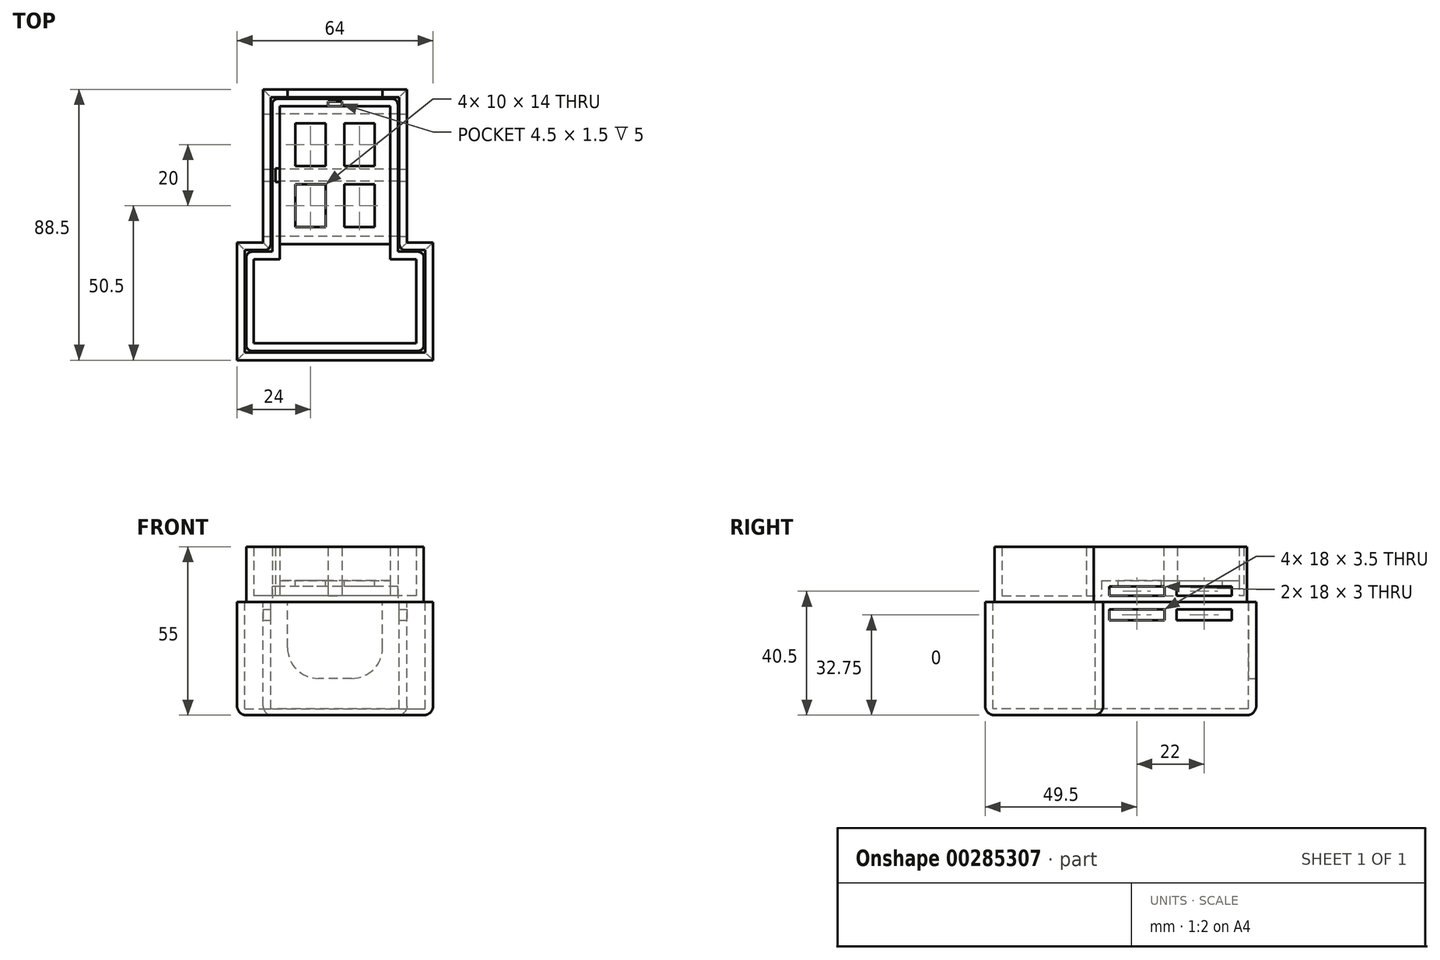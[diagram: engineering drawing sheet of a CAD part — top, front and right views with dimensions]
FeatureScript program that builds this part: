
annotation { "Feature Type Name" : "Feature", "Feature Type Description" : "" }
export const myFeature = defineFeature(function(context is Context, id is Id, definition is map)
    precondition{}
    {
        {
            var Q0;
            Q0=qCreatedBy(makeId("Top.planeOp"),FACE);
            var sketch = newSketch(context, id + "F0", { "sketchPlane" : qUnion([Q0])});
            skLineSegment(sketch, "E0.bottom", {"start": v(20.5, 25) * mm, "end": v(-20.5, 25) * mm});
            skLineSegment(sketch, "E0.left", {"start": v(20.5, 25) * mm, "end": v(20.5, -25) * mm});
            skLineSegment(sketch, "E0.right", {"start": v(-20.5, 25) * mm, "end": v(-20.5, -25) * mm});
            skPoint(sketch, "E0.middle", {"position": v(0, 0) * mm});
            skLineSegment(sketch, "E1.bottom", {"start": v(-29, -25) * mm, "end": v(-20.5, -25) * mm});
            skLineSegment(sketch, "E1.top", {"start": v(-29, -57.5) * mm, "end": v(29, -57.5) * mm});
            skLineSegment(sketch, "E1.left", {"start": v(-29, -25) * mm, "end": v(-29, -57.5) * mm});
            skLineSegment(sketch, "E1.right", {"start": v(29, -25) * mm, "end": v(29, -57.5) * mm});
            skPoint(sketch, "E1.middle", {"position": v(0, -41.25) * mm});
            skLineSegment(sketch, "E2.trimOffspring", {"start": v(20.5, -25) * mm, "end": v(29, -25) * mm});
            skLineSegment(sketch, "E3.0", {"start": v(18, 22.5) * mm, "end": v(2.25, 22.5) * mm});
            skLineSegment(sketch, "E3.1", {"start": v(-18, 22.5) * mm, "end": v(-18, 2.25) * mm});
            skLineSegment(sketch, "E3.2", {"start": v(18, 22.5) * mm, "end": v(18, -27.5) * mm});
            skLineSegment(sketch, "E3.3", {"start": v(-26.5, -27.5) * mm, "end": v(-18, -27.5) * mm});
            skLineSegment(sketch, "E3.4", {"start": v(18, -27.5) * mm, "end": v(26.5, -27.5) * mm});
            skLineSegment(sketch, "E3.5", {"start": v(26.5, -27.5) * mm, "end": v(26.5, -55) * mm});
            skLineSegment(sketch, "E3.6", {"start": v(-26.5, -55) * mm, "end": v(26.5, -55) * mm});
            skLineSegment(sketch, "E3.7", {"start": v(-26.5, -27.5) * mm, "end": v(-26.5, -55) * mm});
            skLineSegment(sketch, "E4.top", {"start": v(-2.25, 24) * mm, "end": v(2.25, 24) * mm});
            skLineSegment(sketch, "E4.left", {"start": v(-2.25, 22.5) * mm, "end": v(-2.25, 24) * mm});
            skLineSegment(sketch, "E4.right", {"start": v(2.25, 22.5) * mm, "end": v(2.25, 24) * mm});
            skLineSegment(sketch, "E5.trimOffspring", {"start": v(-2.25, 22.5) * mm, "end": v(-18, 22.5) * mm});
            skLineSegment(sketch, "E6.bottom", {"start": v(-18, 2.25) * mm, "end": v(-19.5, 2.25) * mm});
            skLineSegment(sketch, "E6.top", {"start": v(-18, -2.25) * mm, "end": v(-19.5, -2.25) * mm});
            skLineSegment(sketch, "E6.right", {"start": v(-19.5, 2.25) * mm, "end": v(-19.5, -2.25) * mm});
            skLineSegment(sketch, "E7.trimOffspring", {"start": v(-18, -2.25) * mm, "end": v(-18, -27.5) * mm});
            skLineSegment(sketch, "E8.0", {"start": v(-29.5, -24.5) * mm, "end": v(-29.5, -58) * mm});
            skLineSegment(sketch, "E8.1", {"start": v(-29.5, -24.5) * mm, "end": v(-23, -24.5) * mm});
            skLineSegment(sketch, "E8.2", {"start": v(-29.5, -58) * mm, "end": v(29.5, -58) * mm});
            skLineSegment(sketch, "E8.3", {"start": v(-21, 25.5) * mm, "end": v(-21, -22.5) * mm});
            skLineSegment(sketch, "E8.4", {"start": v(29.5, -24.5) * mm, "end": v(29.5, -58) * mm});
            skLineSegment(sketch, "E8.5", {"start": v(23, -24.5) * mm, "end": v(29.5, -24.5) * mm});
            skLineSegment(sketch, "E8.6", {"start": v(21, 25.5) * mm, "end": v(21, -22.5) * mm});
            skLineSegment(sketch, "E8.7", {"start": v(21, 25.5) * mm, "end": v(-21, 25.5) * mm});
            skLineSegment(sketch, "E9.0", {"start": v(-32, -22) * mm, "end": v(-32, -60.5) * mm});
            skLineSegment(sketch, "E9.1", {"start": v(-32, -22) * mm, "end": v(-23.5, -22) * mm});
            skLineSegment(sketch, "E9.2", {"start": v(-32, -60.5) * mm, "end": v(32, -60.5) * mm});
            skLineSegment(sketch, "E9.3", {"start": v(-23.5, 28) * mm, "end": v(-23.5, -22) * mm});
            skLineSegment(sketch, "E9.4", {"start": v(32, -22) * mm, "end": v(32, -60.5) * mm});
            skLineSegment(sketch, "E9.5", {"start": v(23.5, -22) * mm, "end": v(32, -22) * mm});
            skLineSegment(sketch, "E9.6", {"start": v(23.5, 28) * mm, "end": v(23.5, -22) * mm});
            skLineSegment(sketch, "E9.7", {"start": v(23.5, 28) * mm, "end": v(-23.5, 28) * mm});
            skPoint(sketch, "E10.visualSharp", {"position": v(-21, -24.5) * mm});
            skArc(sketch, "E10.filletArc", {"start": v(-23, -24.5) * mm, "mid": v(-21.59, -23.91) * mm, "end": v(-21, -22.5) * mm});
            skPoint(sketch, "E11.visualSharp", {"position": v(21, -24.5) * mm});
            skArc(sketch, "E11.filletArc", {"start": v(21, -22.5) * mm, "mid": v(21.59, -23.91) * mm, "end": v(23, -24.5) * mm});
            skSolve(sketch);
        }
        {
            var Q0;
            Q0=makeQuery(id+"F0.imprint","IMPRINT",FACE,{"disambiguationData":[TD([[makeQuery(id+"F0.imprint","IMPRINT",EDGE,{"derivedFrom":sQuery(id+"F0.wireOp",EDGE,"E0.bottom")}),1.0]])]});
            var Q1;
            Q1=makeQuery(id+"F0.imprint","IMPRINT",FACE,{"disambiguationData":[TD([[makeQuery(id+"F0.imprint","IMPRINT",EDGE,{"derivedFrom":sQuery(id+"F0.wireOp",EDGE,"E3.0")}),1.0]])]});
            extrude(context, id + "F1", {"entities" : qUnion([Q0, Q1]), "depth" : 2 * mm});
        }
        {
            var Q0;
            Q0=makeQuery(id+"F0.imprint","IMPRINT",FACE,{"disambiguationData":[TD([[makeQuery(id+"F0.imprint","IMPRINT",EDGE,{"derivedFrom":sQuery(id+"F0.wireOp",EDGE,"E0.bottom")}),1.0]])]});
            extrude(context, id + "F2", {"entities" : qUnion([Q0]), "operationType" : NewBodyOperationType.ADD, "depth" : 18 * mm});
        }
        {
            var Q0;
            Q0=makeQuery(id+"F1.opExtrude","CAP_FACE",FACE,{"disambiguationData":[OSD([sQuery(id+"F0.wireOp",EDGE,"E0.bottom"),sQuery(id+"F0.wireOp",EDGE,"E0.left"),sQuery(id+"F0.wireOp",EDGE,"E0.right"),sQuery(id+"F0.wireOp",EDGE,"E1.bottom"),sQuery(id+"F0.wireOp",EDGE,"E1.top"),sQuery(id+"F0.wireOp",EDGE,"E1.left"),sQuery(id+"F0.wireOp",EDGE,"E1.right"),sQuery(id+"F0.wireOp",EDGE,"E2.trimOffspring")])],"isStart":false});
            var sketch = newSketch(context, id + "F3", { "sketchPlane" : qUnion([Q0])});
            skLineSegment(sketch, "E12.bottom", {"start": v(18, 22.5) * mm, "end": v(-18, 22.5) * mm});
            skLineSegment(sketch, "E12.top", {"start": v(18, -22.5) * mm, "end": v(-18, -22.5) * mm});
            skLineSegment(sketch, "E12.left", {"start": v(18, 22.5) * mm, "end": v(18, -22.5) * mm});
            skLineSegment(sketch, "E12.right", {"start": v(-18, 22.5) * mm, "end": v(-18, -22.5) * mm});
            skPoint(sketch, "E12.middle", {"position": v(0, 0) * mm});
            skSolve(sketch);
        }
        {
            var Q0;
            {var subQ0=sQuery(id+"F3.wireOp",EDGE,"E12.top");Q0=makeQuery(id+"F3.imprint","IMPRINT",FACE,{"disambiguationData":[TD([[makeQuery(id+"F3.imprint","IMPRINT",EDGE,{"derivedFrom":subQ0}),-1.0]])]});}
            extrude(context, id + "F4", {"entities" : qUnion([Q0]), "operationType" : NewBodyOperationType.ADD, "depth" : 5 * mm});
        }
        {
            var Q0;
            {var subQ0=sQuery(id+"F0.wireOp",EDGE,"E0.right");Q0=makeQuery(id+"F2.boolean.opBoolean","MERGE",FACE,{"derivedFrom":[makeQuery(id+"F1.opExtrude","SWEPT_FACE",FACE,{"disambiguationData":[OSD([subQ0])]}),makeQuery(id+"F2.opExtrude","SWEPT_FACE",FACE,{"disambiguationData":[OSD([subQ0])]})]});}
            var sketch = newSketch(context, id + "F5", { "sketchPlane" : qUnion([Q0])});
            skLineSegment(sketch, "E13.bottom", {"start": v(20, 2) * mm, "end": v(2, 2) * mm});
            skLineSegment(sketch, "E13.top", {"start": v(20, 5) * mm, "end": v(2, 5) * mm});
            skLineSegment(sketch, "E13.left", {"start": v(20, 2) * mm, "end": v(20, 5) * mm});
            skLineSegment(sketch, "E13.right", {"start": v(-20, 2) * mm, "end": v(-20, 5) * mm});
            skLineSegment(sketch, "E14", {"start": v(-2, 5) * mm, "end": v(-2, 2) * mm});
            skLineSegment(sketch, "E15", {"start": v(2, 5) * mm, "end": v(2, 2) * mm});
            skLineSegment(sketch, "E16.trimOffspring", {"start": v(-2, 5) * mm, "end": v(-20, 5) * mm});
            skLineSegment(sketch, "E17.trimOffspring", {"start": v(-2, 2) * mm, "end": v(-20, 2) * mm});
            skSolve(sketch);
        }
        {
            var Q0;
            Q0 = qSketchRegion(id + "F5", true);
            var Q1;
            {var subQ0=sQuery(id+"F0.wireOp",EDGE,"E0.left");Q1=makeQuery(id+"F2.boolean.opBoolean","MERGE",FACE,{"derivedFrom":[makeQuery(id+"F1.opExtrude","SWEPT_FACE",FACE,{"disambiguationData":[OSD([subQ0])]}),makeQuery(id+"F2.opExtrude","SWEPT_FACE",FACE,{"disambiguationData":[OSD([subQ0])]})]});}
            extrude(context, id + "F6", {"entities" : qUnion([Q0]), "operationType" : NewBodyOperationType.REMOVE, "endBound" : BoundingType.UP_TO_SURFACE, "oppositeDirection" : true, "endBoundEntityFace" : qUnion([Q1]), "depth" : 25 * mm});
        }
        {
            var Q0;
            Q0=makeQuery(id+"F4.opExtrude","CAP_FACE",FACE,{"disambiguationData":[OSD([sQuery(id+"F3.wireOp",EDGE,"E12.bottom"),sQuery(id+"F3.wireOp",EDGE,"E12.top"),sQuery(id+"F3.wireOp",EDGE,"E12.left"),sQuery(id+"F3.wireOp",EDGE,"E12.right")])],"isStart":false});
            var sketch = newSketch(context, id + "F7", { "sketchPlane" : qUnion([Q0])});
            skLineSegment(sketch, "E18.bottom", {"start": v(-3, 3) * mm, "end": v(-13, 3) * mm});
            skLineSegment(sketch, "E18.top", {"start": v(-3, 17) * mm, "end": v(-13, 17) * mm});
            skLineSegment(sketch, "E18.left", {"start": v(-3, 3) * mm, "end": v(-3, 17) * mm});
            skLineSegment(sketch, "E18.right", {"start": v(-13, 3) * mm, "end": v(-13, 17) * mm});
            skPoint(sketch, "E18.middle", {"position": v(-8, 10) * mm});
            skLineSegment(sketch, "E19.1.0.0", {"start": v(3, 3) * mm, "end": v(3, 17) * mm});
            skPoint(sketch, "E19.1.0.1", {"position": v(8, 10) * mm});
            skLineSegment(sketch, "E19.1.0.2", {"start": v(13, 3) * mm, "end": v(3, 3) * mm});
            skLineSegment(sketch, "E19.1.0.3", {"start": v(13, 3) * mm, "end": v(13, 17) * mm});
            skLineSegment(sketch, "E19.1.0.4", {"start": v(13, 17) * mm, "end": v(3, 17) * mm});
            skLineSegment(sketch, "E19.direction1", {"start": v(-13, 3) * mm, "end": v(3, 3) * mm, "construction": true});
            skLineSegment(sketch, "E20", {"start": v(-14.04, 0) * mm, "end": v(15.05, 0) * mm, "construction": true});
            skLineSegment(sketch, "E21.MirrorCS", {"start": v(-3, -3) * mm, "end": v(-13, -3) * mm});
            skLineSegment(sketch, "E22.MirrorCS", {"start": v(13, -3) * mm, "end": v(13, -17) * mm});
            skLineSegment(sketch, "E23.MirrorCS", {"start": v(-3, -3) * mm, "end": v(-3, -17) * mm});
            skPoint(sketch, "E24.MirrorP", {"position": v(-8, -10) * mm});
            skLineSegment(sketch, "E25.MirrorCS", {"start": v(13, -17) * mm, "end": v(3, -17) * mm});
            skLineSegment(sketch, "E26.MirrorCS", {"start": v(-13, -3) * mm, "end": v(3, -3) * mm, "construction": true});
            skLineSegment(sketch, "E27.MirrorCS", {"start": v(13, -3) * mm, "end": v(3, -3) * mm});
            skLineSegment(sketch, "E28.MirrorCS", {"start": v(3, -3) * mm, "end": v(3, -17) * mm});
            skLineSegment(sketch, "E29.MirrorCS", {"start": v(-13, -3) * mm, "end": v(-13, -17) * mm});
            skLineSegment(sketch, "E30.MirrorCS", {"start": v(-3, -17) * mm, "end": v(-13, -17) * mm});
            skPoint(sketch, "E31.MirrorP", {"position": v(8, -10) * mm});
            skSolve(sketch);
        }
        {
            var Q0;
            Q0 = qSketchRegion(id + "F7", true);
            extrude(context, id + "F8", {"entities" : qUnion([Q0]), "operationType" : NewBodyOperationType.REMOVE, "oppositeDirection" : true, "depth" : 3 * mm});
        }
        {
            var Q0;
            Q0=makeQuery(id+"F0.imprint","IMPRINT",FACE,{"disambiguationData":[TD([[makeQuery(id+"F0.imprint","IMPRINT",EDGE,{"derivedFrom":sQuery(id+"F0.wireOp",EDGE,"E8.0")}),-1.0]])]});
            extrude(context, id + "F9", {"entities" : qUnion([Q0]), "oppositeDirection" : true, "depth" : 35 * mm});
        }
        {
            var Q0;
            Q0=makeQuery(id+"F9.opExtrude","CAP_FACE",FACE,{"disambiguationData":[OSD([sQuery(id+"F0.wireOp",EDGE,"E8.0"),sQuery(id+"F0.wireOp",EDGE,"E8.1"),sQuery(id+"F0.wireOp",EDGE,"E8.2"),sQuery(id+"F0.wireOp",EDGE,"E8.3"),sQuery(id+"F0.wireOp",EDGE,"E8.4"),sQuery(id+"F0.wireOp",EDGE,"E8.5"),sQuery(id+"F0.wireOp",EDGE,"E8.6"),sQuery(id+"F0.wireOp",EDGE,"E8.7"),sQuery(id+"F0.wireOp",EDGE,"E9.0"),sQuery(id+"F0.wireOp",EDGE,"E9.1"),sQuery(id+"F0.wireOp",EDGE,"E9.2"),sQuery(id+"F0.wireOp",EDGE,"E9.3"),sQuery(id+"F0.wireOp",EDGE,"E9.4"),sQuery(id+"F0.wireOp",EDGE,"E9.5"),sQuery(id+"F0.wireOp",EDGE,"E9.6"),sQuery(id+"F0.wireOp",EDGE,"E9.7"),sQuery(id+"F0.wireOp",EDGE,"E10.filletArc"),sQuery(id+"F0.wireOp",EDGE,"E11.filletArc")])],"isStart":false});
            var sketch = newSketch(context, id + "F10", { "sketchPlane" : qUnion([Q0])});
            skLineSegment(sketch, "E32.bottom", {"start": v(-32, 60.5) * mm, "end": v(32, 60.5) * mm});
            skLineSegment(sketch, "E32.top", {"start": v(-23.5, -28) * mm, "end": v(23.5, -28) * mm});
            skLineSegment(sketch, "E32.left", {"start": v(-32, 60.5) * mm, "end": v(-32, 22) * mm});
            skLineSegment(sketch, "E32.right", {"start": v(32, 60.5) * mm, "end": v(32, 22) * mm});
            skLineSegment(sketch, "E33", {"start": v(-32, 22) * mm, "end": v(-23.5, 22) * mm});
            skLineSegment(sketch, "E34", {"start": v(-23.5, 22) * mm, "end": v(-23.5, -28) * mm});
            skLineSegment(sketch, "E35", {"start": v(32, 22) * mm, "end": v(23.5, 22) * mm});
            skLineSegment(sketch, "E36", {"start": v(23.5, 22) * mm, "end": v(23.5, -28) * mm});
            skPoint(sketch, "E37.orphan", {"position": v(32, -28) * mm});
            skSolve(sketch);
        }
        {
            var Q0;
            Q0 = qSketchRegion(id + "F10", true);
            extrude(context, id + "F11", {"entities" : qUnion([Q0]), "operationType" : NewBodyOperationType.ADD, "depth" : 2 * mm});
        }
        {
            var Q0;
            Q0=makeQuery(id+"F11.opExtrude","CAP_FACE",FACE,{"disambiguationData":[OSD([sQuery(id+"F10.wireOp",EDGE,"E32.bottom"),sQuery(id+"F10.wireOp",EDGE,"E32.top"),sQuery(id+"F10.wireOp",EDGE,"E32.left"),sQuery(id+"F10.wireOp",EDGE,"E32.right"),sQuery(id+"F10.wireOp",EDGE,"E33"),sQuery(id+"F10.wireOp",EDGE,"E34"),sQuery(id+"F10.wireOp",EDGE,"E35"),sQuery(id+"F10.wireOp",EDGE,"E36")])],"isStart":false});
            fillet(context, id + "F12", {"entities" : qUnion([Q0]), "radius" : 3 * mm, "tangentPropagation" : true, "allowEdgeOverflow" : false});
        }
        {
            var Q0;
            {var subQ0=sQuery(id+"F0.wireOp",EDGE,"E1.left");var subQ1=sQuery(id+"F0.wireOp",EDGE,"E1.top");Q0=makeQuery(id+"F2.boolean.opBoolean","MERGE",EDGE,{"derivedFrom":[makeQuery(id+"F1.opExtrude","SWEPT_EDGE",EDGE,{"disambiguationData":[OSD([subQ1,subQ0])]}),makeQuery(id+"F2.opExtrude","SWEPT_EDGE",EDGE,{"disambiguationData":[OSD([subQ1,subQ0])]})]});}
            var Q1;
            {var subQ0=sQuery(id+"F0.wireOp",EDGE,"E1.left");var subQ1=sQuery(id+"F0.wireOp",EDGE,"E1.bottom");Q1=makeQuery(id+"F2.boolean.opBoolean","MERGE",EDGE,{"derivedFrom":[makeQuery(id+"F1.opExtrude","SWEPT_EDGE",EDGE,{"disambiguationData":[OSD([subQ1,subQ0])]}),makeQuery(id+"F2.opExtrude","SWEPT_EDGE",EDGE,{"disambiguationData":[OSD([subQ1,subQ0])]})]});}
            var Q2;
            {var subQ0=sQuery(id+"F0.wireOp",EDGE,"E1.right");var subQ1=sQuery(id+"F0.wireOp",EDGE,"E1.top");Q2=makeQuery(id+"F2.boolean.opBoolean","MERGE",EDGE,{"derivedFrom":[makeQuery(id+"F1.opExtrude","SWEPT_EDGE",EDGE,{"disambiguationData":[OSD([subQ1,subQ0])]}),makeQuery(id+"F2.opExtrude","SWEPT_EDGE",EDGE,{"disambiguationData":[OSD([subQ1,subQ0])]})]});}
            var Q3;
            {var subQ0=sQuery(id+"F0.wireOp",EDGE,"E0.right");var subQ1=sQuery(id+"F0.wireOp",EDGE,"E0.bottom");Q3=makeQuery(id+"F2.boolean.opBoolean","MERGE",EDGE,{"derivedFrom":[makeQuery(id+"F1.opExtrude","SWEPT_EDGE",EDGE,{"disambiguationData":[OSD([subQ1,subQ0])]}),makeQuery(id+"F2.opExtrude","SWEPT_EDGE",EDGE,{"disambiguationData":[OSD([subQ1,subQ0])]})]});}
            var Q4;
            {var subQ0=sQuery(id+"F0.wireOp",EDGE,"E2.trimOffspring");var subQ1=sQuery(id+"F0.wireOp",EDGE,"E1.right");Q4=makeQuery(id+"F2.boolean.opBoolean","MERGE",EDGE,{"derivedFrom":[makeQuery(id+"F1.opExtrude","SWEPT_EDGE",EDGE,{"disambiguationData":[OSD([subQ1,subQ0])]}),makeQuery(id+"F2.opExtrude","SWEPT_EDGE",EDGE,{"disambiguationData":[OSD([subQ1,subQ0])]})]});}
            var Q5;
            {var subQ0=sQuery(id+"F0.wireOp",EDGE,"E0.left");var subQ1=sQuery(id+"F0.wireOp",EDGE,"E0.bottom");Q5=makeQuery(id+"F2.boolean.opBoolean","MERGE",EDGE,{"derivedFrom":[makeQuery(id+"F1.opExtrude","SWEPT_EDGE",EDGE,{"disambiguationData":[OSD([subQ1,subQ0])]}),makeQuery(id+"F2.opExtrude","SWEPT_EDGE",EDGE,{"disambiguationData":[OSD([subQ1,subQ0])]})]});}
            fillet(context, id + "F13", {"entities" : qUnion([Q0, Q1, Q2, Q3, Q4, Q5]), "radius" : 2 * mm, "tangentPropagation" : true, "allowEdgeOverflow" : false});
        }
        {
            var Q0;
            Q0=makeQuery(id+"F11.boolean.opBoolean","MERGE",FACE,{"derivedFrom":[makeQuery(id+"F9.opExtrude","SWEPT_FACE",FACE,{"disambiguationData":[OSD([sQuery(id+"F0.wireOp",EDGE,"E9.7")])]}),makeQuery(id+"F11.opExtrude","SWEPT_FACE",FACE,{"disambiguationData":[OSD([sQuery(id+"F10.wireOp",EDGE,"E32.top")])]})]});
            var sketch = newSketch(context, id + "F14", { "sketchPlane" : qUnion([Q0])});
            skLineSegment(sketch, "E38.top", {"start": v(-15.5, 0) * mm, "end": v(15.5, 0) * mm});
            skLineSegment(sketch, "E38.left", {"start": v(-15.5, -25) * mm, "end": v(-15.5, 0) * mm});
            skLineSegment(sketch, "E38.right", {"start": v(15.5, -25) * mm, "end": v(15.5, 0) * mm});
            skLineSegment(sketch, "E39", {"start": v(-15.5, -25) * mm, "end": v(15.5, -25) * mm});
            skSolve(sketch);
        }
        {
            var Q0;
            Q0 = qSketchRegion(id + "F14", true);
            var Q1;
            Q1=makeQuery(id+"F9.opExtrude","SWEPT_FACE",FACE,{"disambiguationData":[OSD([sQuery(id+"F0.wireOp",EDGE,"E8.7")])]});
            extrude(context, id + "F15", {"entities" : qUnion([Q0]), "operationType" : NewBodyOperationType.REMOVE, "endBound" : BoundingType.UP_TO_SURFACE, "oppositeDirection" : true, "endBoundEntityFace" : qUnion([Q1]), "depth" : 25 * mm});
        }
        {
            var Q0;
            Q0=makeQuery(id+"F11.boolean.opBoolean","MERGE",FACE,{"derivedFrom":[makeQuery(id+"F9.opExtrude","SWEPT_FACE",FACE,{"disambiguationData":[OSD([sQuery(id+"F0.wireOp",EDGE,"E9.6")])]}),makeQuery(id+"F11.opExtrude","SWEPT_FACE",FACE,{"disambiguationData":[OSD([sQuery(id+"F10.wireOp",EDGE,"E36")])]})]});
            var sketch = newSketch(context, id + "F16", { "sketchPlane" : qUnion([Q0])});
            skLineSegment(sketch, "E40", {"start": v(0, 0) * mm, "end": v(0, -11.42) * mm, "construction": true});
            skLineSegment(sketch, "E41.bottom", {"start": v(-20, -2.5) * mm, "end": v(-2, -2.5) * mm});
            skLineSegment(sketch, "E41.top", {"start": v(-20, -6) * mm, "end": v(-2, -6) * mm});
            skLineSegment(sketch, "E41.left", {"start": v(-20, -2.5) * mm, "end": v(-20, -6) * mm});
            skLineSegment(sketch, "E41.right", {"start": v(-2, -2.5) * mm, "end": v(-2, -6) * mm});
            skLineSegment(sketch, "E42.MirrorCS", {"start": v(20, -2.5) * mm, "end": v(20, -6) * mm});
            skLineSegment(sketch, "E43.MirrorCS", {"start": v(20, -6) * mm, "end": v(2, -6) * mm});
            skLineSegment(sketch, "E44.MirrorCS", {"start": v(2, -2.5) * mm, "end": v(2, -6) * mm});
            skLineSegment(sketch, "E45.MirrorCS", {"start": v(20, -2.5) * mm, "end": v(2, -2.5) * mm});
            skSolve(sketch);
        }
        {
            var Q0;
            Q0 = qSketchRegion(id + "F16", true);
            var Q1;
            Q1=makeQuery(id+"F11.boolean.opBoolean","MERGE",FACE,{"derivedFrom":[makeQuery(id+"F9.opExtrude","SWEPT_FACE",FACE,{"disambiguationData":[OSD([sQuery(id+"F0.wireOp",EDGE,"E9.3")])]}),makeQuery(id+"F11.opExtrude","SWEPT_FACE",FACE,{"disambiguationData":[OSD([sQuery(id+"F10.wireOp",EDGE,"E34")])]})]});
            extrude(context, id + "F17", {"entities" : qUnion([Q0]), "operationType" : NewBodyOperationType.REMOVE, "endBound" : BoundingType.UP_TO_SURFACE, "oppositeDirection" : true, "endBoundEntityFace" : qUnion([Q1]), "depth" : 25 * mm});
        }
        {
            var Q0;
            Q0=makeQuery(id+"F15.boolean.opBoolean","COPY",EDGE,{"derivedFrom":makeQuery(id+"F15.opExtrude","SWEPT_EDGE",EDGE,{"disambiguationData":[OSD([sQuery(id+"F14.wireOp",EDGE,"E38.left"),sQuery(id+"F14.wireOp",EDGE,"E39")])]})});
            var Q1;
            Q1=makeQuery(id+"F15.boolean.opBoolean","COPY",EDGE,{"derivedFrom":makeQuery(id+"F15.opExtrude","SWEPT_EDGE",EDGE,{"disambiguationData":[OSD([sQuery(id+"F14.wireOp",EDGE,"E38.right"),sQuery(id+"F14.wireOp",EDGE,"E39")])]})});
            fillet(context, id + "F18", {"entities" : qUnion([Q0, Q1]), "radius" : 10 * mm, "tangentPropagation" : true, "allowEdgeOverflow" : false});
        }
    });
